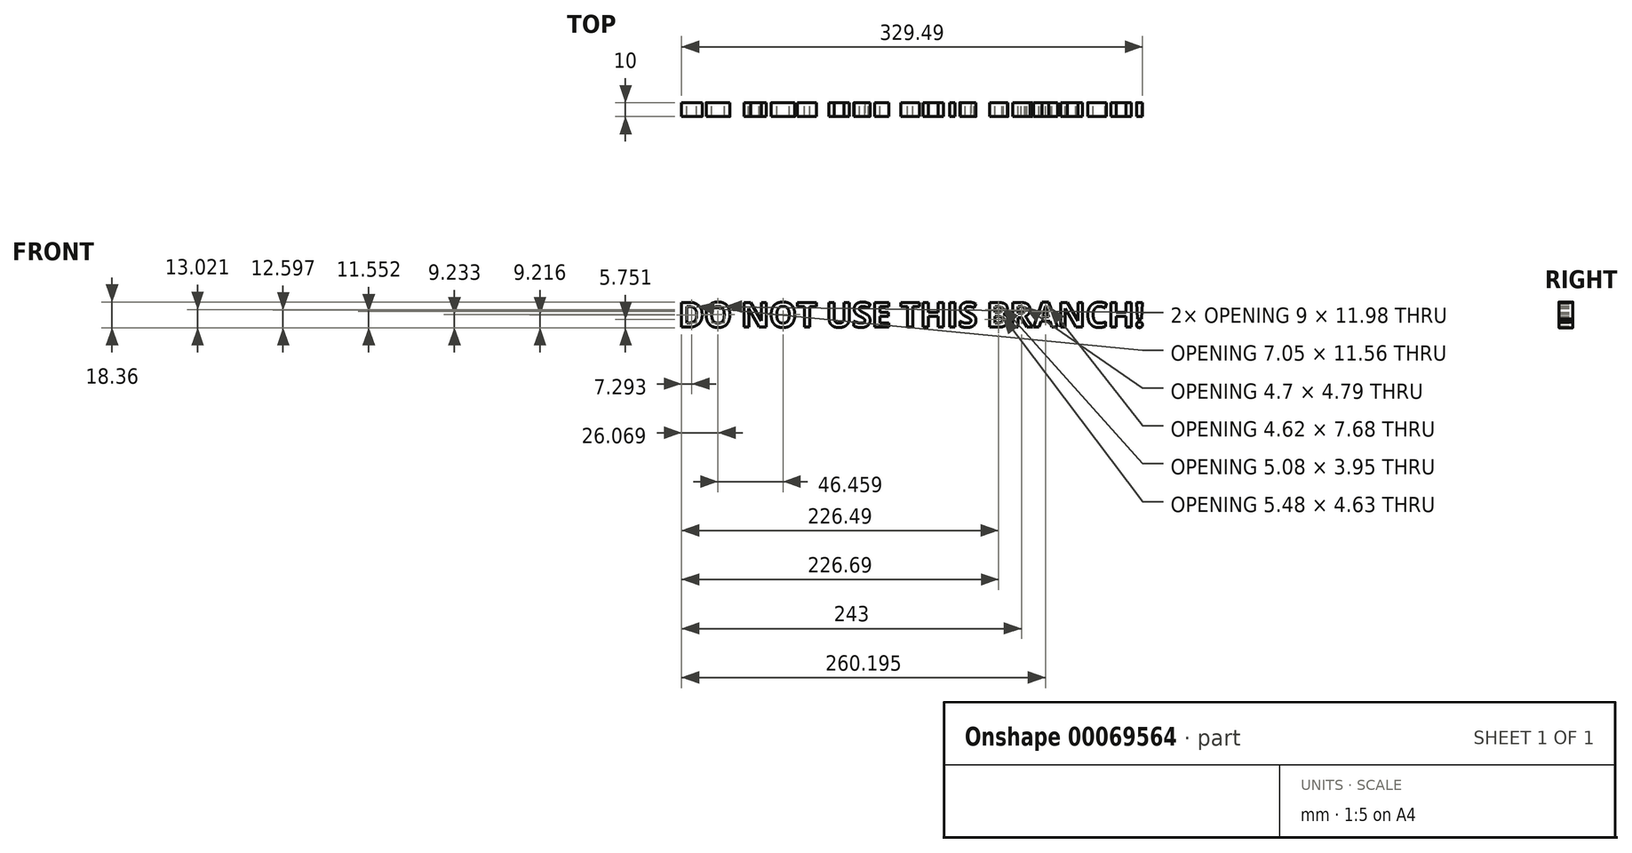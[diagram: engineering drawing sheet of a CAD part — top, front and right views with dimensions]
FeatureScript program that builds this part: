
annotation { "Feature Type Name" : "Feature", "Feature Type Description" : "" }
export const myFeature = defineFeature(function(context is Context, id is Id, definition is map)
    precondition{}
    {
        {
            var Q0;
            Q0=qCreatedBy(makeId("Front.planeOp"),FACE);
            var sketch = newSketch(context, id + "F0", { "sketchPlane" : qUnion([Q0])});
            skText(sketch, "E0", { "text": "DO NOT USE THIS BRANCH!", "fontName": "OpenSans-Bold.ttf"});
            const initialGuessF0  = {"E0": [-0.14531, 0.03509, 1, 0, 0.0179]};
            skSetInitialGuess(sketch, initialGuessF0);
            skSolve(sketch);
        }
        {
            var Q0;
            Q0 = qSketchRegion(id + "F0", true);
            extrude(context, id + "F1", {"entities" : qUnion([Q0]), "depth" : 10 * mm});
        }
    });
